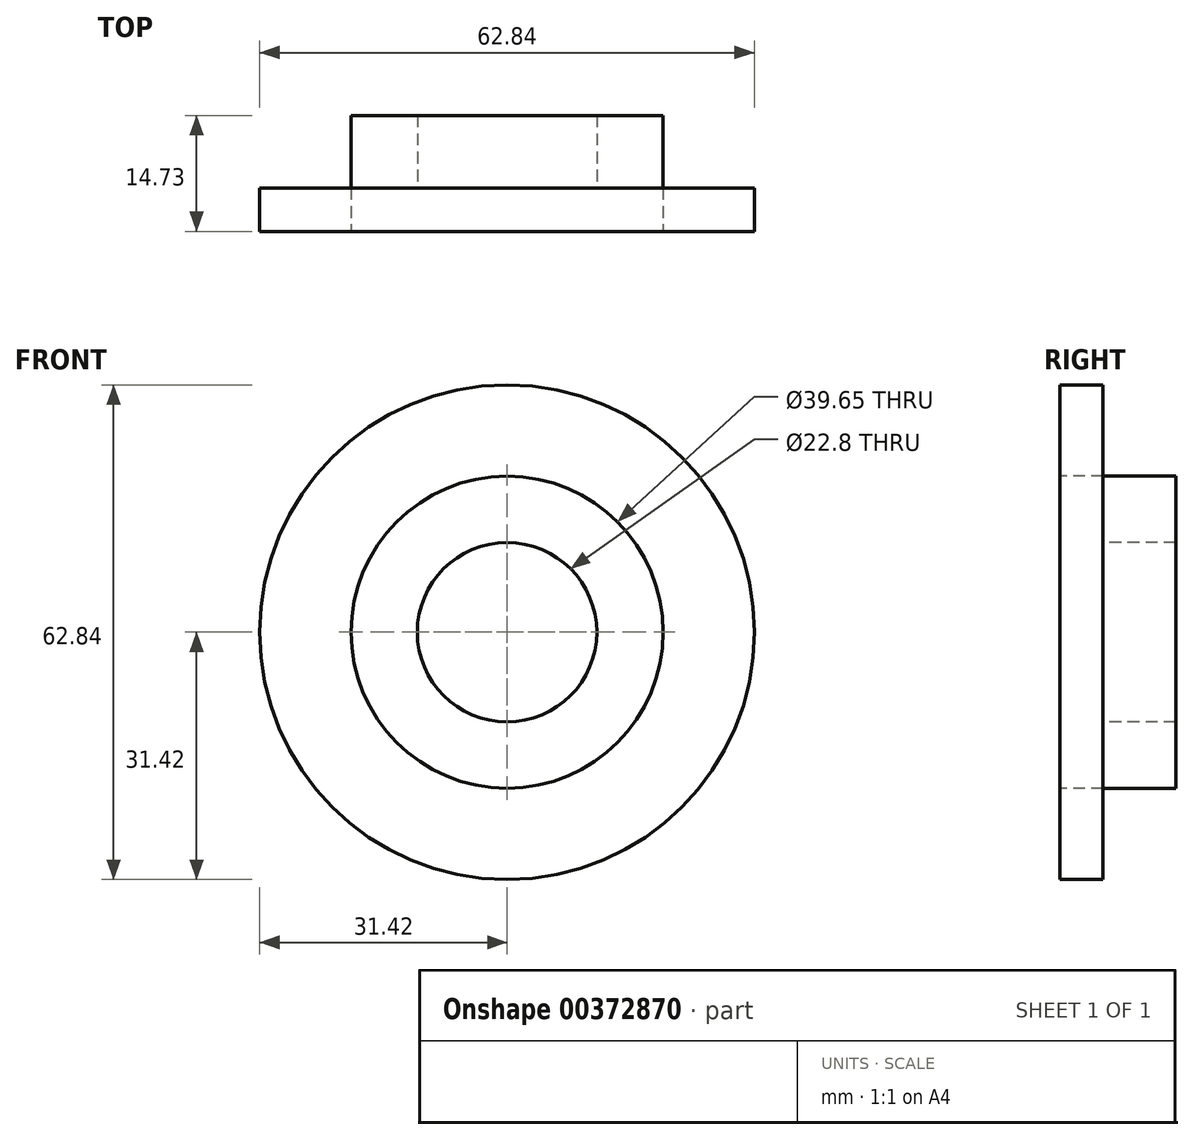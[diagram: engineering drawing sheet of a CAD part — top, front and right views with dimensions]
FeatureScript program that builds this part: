
annotation { "Feature Type Name" : "Feature", "Feature Type Description" : "" }
export const myFeature = defineFeature(function(context is Context, id is Id, definition is map)
    precondition{}
    {
        {
            var Q0;
            Q0=qCreatedBy(makeId("Right.planeOp"),FACE);
            var sketch = newSketch(context, id + "F0", { "sketchPlane" : qUnion([Q0])});
            skLineSegment(sketch, "E0", {"start": v(0, 0) * mm, "end": v(14.7, 0) * mm, "construction": true});
            skLineSegment(sketch, "E1.bottom", {"start": v(0, 11.4) * mm, "end": v(5.52, 11.4) * mm});
            skLineSegment(sketch, "E1.top", {"start": v(0, 31.42) * mm, "end": v(5.52, 31.42) * mm});
            skLineSegment(sketch, "E1.left", {"start": v(0, 11.4) * mm, "end": v(0, 31.42) * mm});
            skLineSegment(sketch, "E1.right", {"start": v(5.52, 11.4) * mm, "end": v(5.52, 31.42) * mm});
            skLineSegment(sketch, "E2.bottom", {"start": v(0, 19.82) * mm, "end": v(14.73, 19.82) * mm});
            skLineSegment(sketch, "E2.top", {"start": v(0, 11.4) * mm, "end": v(14.73, 11.4) * mm});
            skLineSegment(sketch, "E2.left", {"start": v(0, 19.82) * mm, "end": v(0, 11.4) * mm});
            skLineSegment(sketch, "E2.right", {"start": v(14.73, 19.82) * mm, "end": v(14.73, 11.4) * mm});
            skLineSegment(sketch, "E3.MirrorCS", {"start": v(0, -11.4) * mm, "end": v(5.52, -11.4) * mm});
            skLineSegment(sketch, "E4.MirrorCS", {"start": v(14.73, -19.82) * mm, "end": v(14.73, -11.4) * mm});
            skLineSegment(sketch, "E5.MirrorCS", {"start": v(0, -19.82) * mm, "end": v(0, -11.4) * mm});
            skLineSegment(sketch, "E6.MirrorCS", {"start": v(0, -31.42) * mm, "end": v(5.52, -31.42) * mm});
            skLineSegment(sketch, "E7.MirrorCS", {"start": v(0, -11.4) * mm, "end": v(0, -31.42) * mm});
            skLineSegment(sketch, "E8.MirrorCS", {"start": v(5.52, -11.4) * mm, "end": v(5.52, -31.42) * mm});
            skLineSegment(sketch, "E9.MirrorCS", {"start": v(0, -19.82) * mm, "end": v(14.73, -19.82) * mm});
            skLineSegment(sketch, "E10.MirrorCS", {"start": v(0, -11.4) * mm, "end": v(14.73, -11.4) * mm});
            skSolve(sketch);
        }
        {
            var Q0;
            {var subQ0=sQuery(id+"F0.wireOp",EDGE,"E1.top");Q0=makeQuery(id+"F0.imprint","IMPRINT",FACE,{"disambiguationData":[TD([[makeQuery(id+"F0.imprint","IMPRINT",EDGE,{"derivedFrom":subQ0}),-1.0]])]});}
            var Q1;
            {var subQ5=sQuery(id+"F0.wireOp",EDGE,"E2.right");Q1=makeQuery(id+"F0.imprint","IMPRINT",FACE,{"disambiguationData":[TD([[makeQuery(id+"F0.imprint","IMPRINT",EDGE,{"derivedFrom":subQ5}),-1.0]])]});}
            var Q2;
            {var subQ5=sQuery(id+"F0.wireOp",EDGE,"E2.left");Q2=makeQuery(id+"F0.imprint","IMPRINT",FACE,{"disambiguationData":[TD([[makeQuery(id+"F0.imprint","IMPRINT",EDGE,{"derivedFrom":subQ5}),1.0]])]});}
            var Q3;
            Q3=sQuery(id+"F0.wireOp",EDGE,"E0");
            revolve(context, id + "F1", {"entities" : qUnion([Q0, Q1, Q2]), "axis" : qUnion([Q3]), "revolveType" : RevolveType.FULL});
        }
    });
